# Revit family: Sump unit draft 24-5-16 6
name_source: partatom
category: Generic Models
revit_build: Autodesk Revit 2014 (Build: 20130308_1515(x64)
units: mm (PartAtom-declared; Revit-internal decimal feet)

## types (3) — shared parameters
Abmessungen = 500mm x 135mm x 460mm (LxWxH)
Anschrift = Postfach 320, 24755 Rendsburg
Artikelnummer = 132391
Assembly Code = D2040
Belastungsklasse = A 15 - E 600
Beschreibung = Entwässerungsrinne
Betreibs- und Wartungshinweise = http://www.aco-tiefbau.de
Breite = 135 mm  [stored 0.442913 ft]
Deponierfähigkeit Material Rinnenkörper = Abfallschlüssel 170107 gem. Verordnung über das Europäische Abfallverzeichnis
Einbauempfehlung, Qualität und Menge Ummantelungsbeton = http://www.aco-tiefbau.de
Einbauempfehlungen = http://www.aco-tiefbau.de
Farbe Kantenschutz = silber
Farbe Rinnenkörper = braun
Fax = +40 (0) 4331 354358
Gewicht = 26.9 Kg
Höhe = 460 mm  [stored 1.50919 ft]
Length = 500 mm  [stored 1.64042 ft]
Lieferant = ACO Tiefbau Vertrieb GmbH
Länge = 500 mm  [stored 1.64042 ft]
Material Kantenschutz = Stahl
Material Rinnenkörper = ACO Polymerbeton
Norm = DIN EN 1433:2002, CE - Kennzeichnung
Oberflächenschutz Kantenschutz = verzinkt
Preis / Stck = http://www.aco-tiefbau.de
Produktbroschüre = http://www.aco-tiefbau.de
Produktinformationen = http://www.aco-tiefbau.de
Produktname = ACO DRAIN Multiline V 100 S
Recyclingfähigkeit Material Kantenschutz = voll recyclingfähig
Recyclingfähigkeit Material Rinnenkörper = voll recyclingfähig
Telefon = +49 (0) 4331 354 500
Type Comments = ACO DRAIN Multiline Einlaufkasten, 500mm lang, mit Lippenlabyrinthdichtung aus NBR DN/OD 110 für horizontalen, wasserdichten Rohranschluss,mit Anschlussadaptern für wasserdichten Rinnenanschluss
URL = www.aco-tiefbau.de
Version = 1
entwickelt von = www.aco-tiefbau.de
hydraulische Leistungsfähigkeit = e_mail anwendungstechnik

## per-type parameters (varying)
| type | Adapter clear ht | Adapter ht |
| Sump unit-Channel type 0 | 97.75 mm | 165 mm  [stored 0.541339 ft] |
| Sump unit-Channel type 5 | 122.75 mm  [stored 0.402723 ft] | 190 mm  [stored 0.62336 ft] |
| Sump unit-Channel type 10 | 137.75 mm  [stored 0.451936 ft] | 215 mm  [stored 0.705381 ft] |

note: [stored X ft] marks values corroborated as IEEE doubles in the binary element streams (Revit-internal decimal feet)

## geometry (parser evidence)
native form markers: Sweep x13
no freeform markers — native parametric forms only
